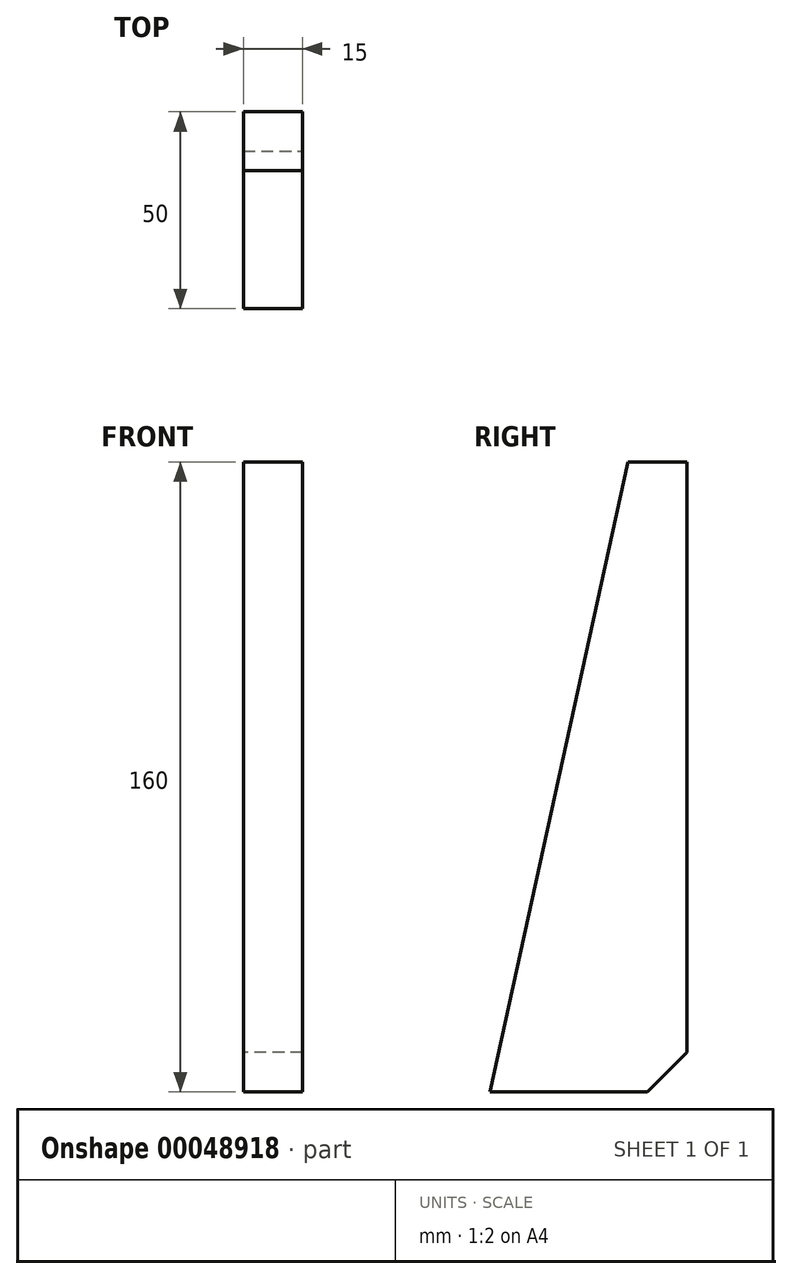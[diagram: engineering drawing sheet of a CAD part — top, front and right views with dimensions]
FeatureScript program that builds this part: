
annotation { "Feature Type Name" : "Feature", "Feature Type Description" : "" }
export const myFeature = defineFeature(function(context is Context, id is Id, definition is map)
    precondition{}
    {
        {
            var Q0;
            Q0=qCreatedBy(makeId("Right.planeOp"),FACE);
            var sketch = newSketch(context, id + "F0", { "sketchPlane" : qUnion([Q0])});
            skLineSegment(sketch, "E0", {"start": v(0, 0) * mm, "end": v(50, 0) * mm});
            skLineSegment(sketch, "E1", {"start": v(50, 0) * mm, "end": v(50, 160) * mm});
            skLineSegment(sketch, "E2", {"start": v(50, 160) * mm, "end": v(35, 160) * mm});
            skLineSegment(sketch, "E3", {"start": v(35, 160) * mm, "end": v(0, 0) * mm});
            skSolve(sketch);
        }
        {
            var Q0;
            Q0=makeQuery(id+"F0.imprint","IMPRINT",FACE,{"disambiguationData":[TD([[makeQuery(id+"F0.imprint","IMPRINT",EDGE,{"derivedFrom":sQuery(id+"F0.wireOp",EDGE,"E0")}),1.0]])]});
            extrude(context, id + "F1", {"entities" : qUnion([Q0]), "depth" : 15 * mm});
        }
        {
            var Q0;
            Q0=makeQuery(id+"F1.opExtrude","SWEPT_EDGE",EDGE,{"disambiguationData":[OSD([sQuery(id+"F0.wireOp",EDGE,"E0"),sQuery(id+"F0.wireOp",EDGE,"E1")])]});
            chamfer(context, id + "F2", {"entities" : qUnion([Q0]), "chamferType" : ChamferType.OFFSET_ANGLE, "width" : 10 * mm, "oppositeDirection" : false, "angle" : 45 * degree, "tangentPropagation" : true});
        }
    });
